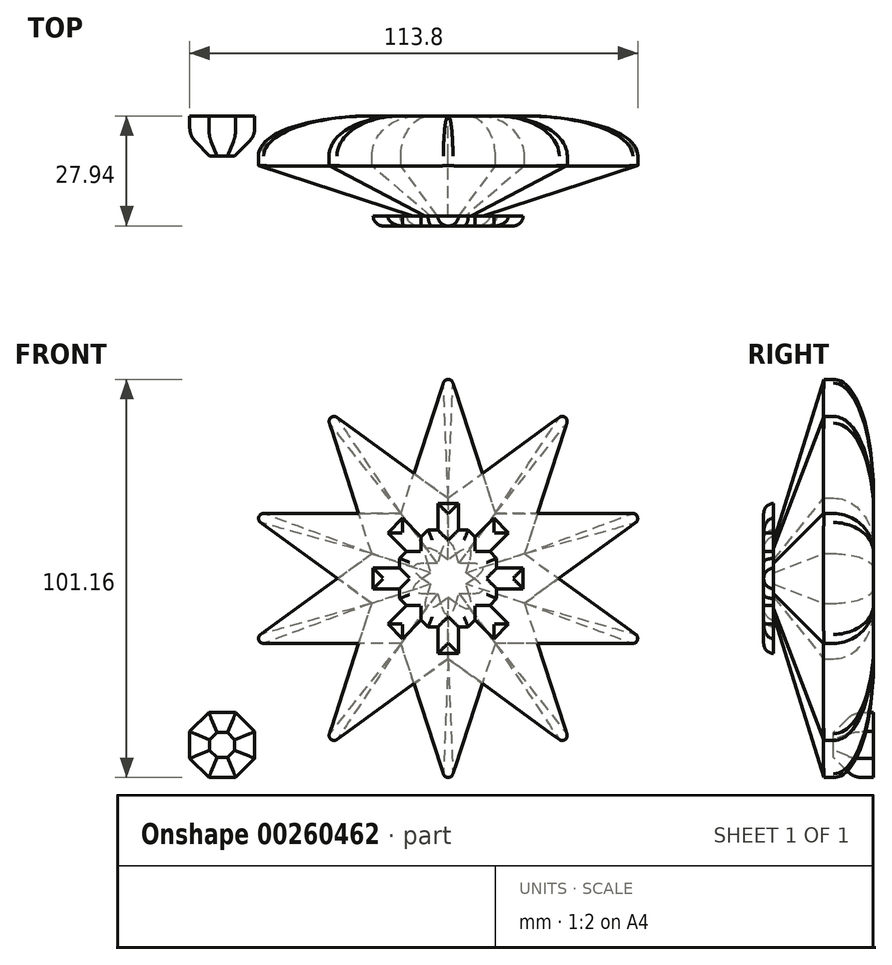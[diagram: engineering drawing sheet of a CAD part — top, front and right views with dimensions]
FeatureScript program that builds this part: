
annotation { "Feature Type Name" : "Feature", "Feature Type Description" : "" }
export const myFeature = defineFeature(function(context is Context, id is Id, definition is map)
    precondition{}
    {
        {
            var Q0;
            Q0=qCreatedBy(makeId("Front.planeOp"),FACE);
            var sketch = newSketch(context, id + "F0", { "sketchPlane" : qUnion([Q0])});
            skPoint(sketch, "E0.0.midPoint", {"position": v(0, 43.21) * mm});
            skLineSegment(sketch, "E1", {"start": v(50.8, -16.5) * mm, "end": v(-50.8, -16.5) * mm});
            skLineSegment(sketch, "E2", {"start": v(-50.8, -16.5) * mm, "end": v(31.4, 43.21) * mm});
            skLineSegment(sketch, "E3", {"start": v(31.4, 43.21) * mm, "end": v(0, -53.41) * mm});
            skLineSegment(sketch, "E4", {"start": v(0, -53.41) * mm, "end": v(-31.4, 43.21) * mm});
            skLineSegment(sketch, "E5", {"start": v(-31.4, 43.21) * mm, "end": v(50.8, -16.5) * mm});
            skSolve(sketch);
        }
        {
            var Q0;
            Q0=qCreatedBy(makeId("Front.planeOp"),FACE);
            var sketch = newSketch(context, id + "F1", { "sketchPlane" : qUnion([Q0])});
            skPoint(sketch, "E6.0.midPoint", {"position": v(0, -43.21) * mm});
            skLineSegment(sketch, "E7", {"start": v(-31.4, -43.21) * mm, "end": v(0, 53.41) * mm});
            skLineSegment(sketch, "E8", {"start": v(0, 53.41) * mm, "end": v(31.4, -43.21) * mm});
            skLineSegment(sketch, "E9", {"start": v(-50.8, 16.5) * mm, "end": v(31.4, -43.21) * mm});
            skLineSegment(sketch, "E10", {"start": v(50.8, 16.5) * mm, "end": v(-50.8, 16.5) * mm});
            skLineSegment(sketch, "E11", {"start": v(-31.4, -43.21) * mm, "end": v(50.8, 16.5) * mm});
            skSolve(sketch);
        }
        {
            var Q0;
            {var subQ0=sQuery(id+"F0.wireOp",EDGE,"E2");var subQ1=sQuery(id+"F0.wireOp",EDGE,"E1");var subQ2=makeQuery(id+"F0.imprint","INTERSECT",VERTEX,{"derivedFrom":[subQ1,subQ0]});Q0=makeQuery(id+"F0.imprint","IMPRINT",FACE,{"disambiguationData":[TD([[makeQuery(id+"F0.imprint","IMPRINT",EDGE,{"disambiguationData":[TD([[subQ2,1.0]])],"derivedFrom":subQ1}),-1.0]])]});}
            var Q1;
            {var subQ0=sQuery(id+"F0.wireOp",EDGE,"E4");var subQ1=sQuery(id+"F0.wireOp",EDGE,"E2");var subQ2=makeQuery(id+"F0.imprint","INTERSECT",VERTEX,{"derivedFrom":[subQ1,subQ0]});Q1=makeQuery(id+"F0.imprint","IMPRINT",FACE,{"disambiguationData":[TD([[makeQuery(id+"F0.imprint","IMPRINT",EDGE,{"disambiguationData":[TD([[subQ2,-1.0]])],"derivedFrom":subQ1}),1.0]])]});}
            var Q2;
            {var subQ1=sQuery(id+"F0.wireOp",EDGE,"E1");var subQ5=sQuery(id+"F0.wireOp",EDGE,"E3");var subQ6=makeQuery(id+"F0.imprint","INTERSECT",VERTEX,{"derivedFrom":[subQ1,subQ5]});Q2=makeQuery(id+"F0.imprint","IMPRINT",FACE,{"disambiguationData":[TD([[makeQuery(id+"F0.imprint","IMPRINT",EDGE,{"disambiguationData":[TD([[subQ6,-1.0]])],"derivedFrom":subQ1}),-1.0]])]});}
            var Q3;
            {var subQ0=sQuery(id+"F0.wireOp",EDGE,"E3");var subQ1=sQuery(id+"F0.wireOp",EDGE,"E2");var subQ2=makeQuery(id+"F0.imprint","INTERSECT",VERTEX,{"derivedFrom":[subQ1,subQ0]});Q3=makeQuery(id+"F0.imprint","IMPRINT",FACE,{"disambiguationData":[TD([[makeQuery(id+"F0.imprint","IMPRINT",EDGE,{"disambiguationData":[TD([[subQ2,1.0]])],"derivedFrom":subQ1}),-1.0]])]});}
            var Q4;
            {var subQ0=sQuery(id+"F0.wireOp",EDGE,"E5");var subQ1=sQuery(id+"F0.wireOp",EDGE,"E1");var subQ2=makeQuery(id+"F0.imprint","INTERSECT",VERTEX,{"derivedFrom":[subQ1,subQ0]});Q4=makeQuery(id+"F0.imprint","IMPRINT",FACE,{"disambiguationData":[TD([[makeQuery(id+"F0.imprint","IMPRINT",EDGE,{"disambiguationData":[TD([[subQ2,-1.0]])],"derivedFrom":subQ1}),-1.0]])]});}
            var Q5;
            {var subQ0=sQuery(id+"F0.wireOp",EDGE,"E3");var subQ1=sQuery(id+"F0.wireOp",EDGE,"E1");var subQ2=makeQuery(id+"F0.imprint","INTERSECT",VERTEX,{"derivedFrom":[subQ1,subQ0]});Q5=makeQuery(id+"F0.imprint","IMPRINT",FACE,{"disambiguationData":[TD([[makeQuery(id+"F0.imprint","IMPRINT",EDGE,{"disambiguationData":[TD([[subQ2,-1.0]])],"derivedFrom":subQ1}),1.0]])]});}
            extrude(context, id + "F2", {"entities" : qUnion([Q0, Q1, Q2, Q3, Q4, Q5]), "depth" : 25.4 * mm});
        }
        {
            var Q0;
            Q0=makeQuery(id+"F2.opExtrude","CAP_FACE",FACE,{"disambiguationData":[OSD([sQuery(id+"F0.wireOp",EDGE,"E1"),sQuery(id+"F0.wireOp",EDGE,"E2"),sQuery(id+"F0.wireOp",EDGE,"E3"),sQuery(id+"F0.wireOp",EDGE,"E4"),sQuery(id+"F0.wireOp",EDGE,"E5")])],"isStart":false});
            chamfer(context, id + "F3", {"entities" : qUnion([Q0]), "width" : 12.7 * mm, "tangentPropagation" : true});
        }
        {
            var Q0;
            {var subQ1=sQuery(id+"F1.wireOp",EDGE,"E7");var subQ7=sQuery(id+"F1.wireOp",EDGE,"E9");var subQ9=makeQuery(id+"F1.imprint","INTERSECT",VERTEX,{"derivedFrom":[subQ1,subQ7]});Q0=makeQuery(id+"F1.imprint","IMPRINT",FACE,{"disambiguationData":[TD([[makeQuery(id+"F1.imprint","IMPRINT",EDGE,{"disambiguationData":[TD([[subQ9,-1.0]])],"derivedFrom":subQ1}),-1.0]])]});}
            var Q1;
            {var subQ0=sQuery(id+"F1.wireOp",EDGE,"E10");var subQ1=sQuery(id+"F1.wireOp",EDGE,"E8");var subQ2=makeQuery(id+"F1.imprint","INTERSECT",VERTEX,{"derivedFrom":[subQ1,subQ0]});Q1=makeQuery(id+"F1.imprint","IMPRINT",FACE,{"disambiguationData":[TD([[makeQuery(id+"F1.imprint","IMPRINT",EDGE,{"disambiguationData":[TD([[subQ2,-1.0]])],"derivedFrom":subQ1}),1.0]])]});}
            var Q2;
            {var subQ0=sQuery(id+"F1.wireOp",EDGE,"E8");var subQ1=sQuery(id+"F1.wireOp",EDGE,"E7");var subQ2=makeQuery(id+"F1.imprint","INTERSECT",VERTEX,{"derivedFrom":[subQ1,subQ0]});Q2=makeQuery(id+"F1.imprint","IMPRINT",FACE,{"disambiguationData":[TD([[makeQuery(id+"F1.imprint","IMPRINT",EDGE,{"disambiguationData":[TD([[subQ2,1.0]])],"derivedFrom":subQ1}),-1.0]])]});}
            var Q3;
            {var subQ0=sQuery(id+"F1.wireOp",EDGE,"E9");var subQ1=sQuery(id+"F1.wireOp",EDGE,"E7");var subQ2=makeQuery(id+"F1.imprint","INTERSECT",VERTEX,{"derivedFrom":[subQ1,subQ0]});Q3=makeQuery(id+"F1.imprint","IMPRINT",FACE,{"disambiguationData":[TD([[makeQuery(id+"F1.imprint","IMPRINT",EDGE,{"disambiguationData":[TD([[subQ2,-1.0]])],"derivedFrom":subQ1}),1.0]])]});}
            var Q4;
            {var subQ0=sQuery(id+"F1.wireOp",EDGE,"E11");var subQ1=sQuery(id+"F1.wireOp",EDGE,"E7");var subQ2=makeQuery(id+"F1.imprint","INTERSECT",VERTEX,{"derivedFrom":[subQ1,subQ0]});Q4=makeQuery(id+"F1.imprint","IMPRINT",FACE,{"disambiguationData":[TD([[makeQuery(id+"F1.imprint","IMPRINT",EDGE,{"disambiguationData":[TD([[subQ2,-1.0]])],"derivedFrom":subQ1}),-1.0]])]});}
            var Q5;
            {var subQ0=sQuery(id+"F1.wireOp",EDGE,"E9");var subQ1=sQuery(id+"F1.wireOp",EDGE,"E8");var subQ2=makeQuery(id+"F1.imprint","INTERSECT",VERTEX,{"derivedFrom":[subQ1,subQ0]});Q5=makeQuery(id+"F1.imprint","IMPRINT",FACE,{"disambiguationData":[TD([[makeQuery(id+"F1.imprint","IMPRINT",EDGE,{"disambiguationData":[TD([[subQ2,1.0]])],"derivedFrom":subQ1}),-1.0]])]});}
            extrude(context, id + "F4", {"entities" : qUnion([Q0, Q1, Q2, Q3, Q4, Q5]), "depth" : 25.4 * mm});
        }
        {
            var Q0;
            Q0=makeQuery(id+"F4.opExtrude","CAP_FACE",FACE,{"disambiguationData":[OSD([sQuery(id+"F1.wireOp",EDGE,"E7"),sQuery(id+"F1.wireOp",EDGE,"E8"),sQuery(id+"F1.wireOp",EDGE,"E9"),sQuery(id+"F1.wireOp",EDGE,"E10"),sQuery(id+"F1.wireOp",EDGE,"E11")])],"isStart":false});
            chamfer(context, id + "F5", {"entities" : qUnion([Q0]), "width" : 12.7 * mm, "tangentPropagation" : true});
        }
        {
            var Q0;
            Q0=makeQuery(id+"F4.opExtrude","CAP_FACE",FACE,{"disambiguationData":[OSD([sQuery(id+"F1.wireOp",EDGE,"E7"),sQuery(id+"F1.wireOp",EDGE,"E8"),sQuery(id+"F1.wireOp",EDGE,"E9"),sQuery(id+"F1.wireOp",EDGE,"E10"),sQuery(id+"F1.wireOp",EDGE,"E11")])],"isStart":false});
            var sketch = newSketch(context, id + "F6", { "sketchPlane" : qUnion([Q0])});
            skCircle(sketch, "E12.cCircle", {"center": v(0, 0) * mm, "radius": 12.32 * mm, "construction": true});
            skLineSegment(sketch, "E12.0", {"start": v(-5.1, 12.32) * mm, "end": v(5.1, 12.32) * mm});
            skLineSegment(sketch, "E12.1", {"start": v(5.1, 12.32) * mm, "end": v(12.32, 5.1) * mm});
            skLineSegment(sketch, "E12.2", {"start": v(12.32, 5.1) * mm, "end": v(12.32, -5.1) * mm});
            skLineSegment(sketch, "E12.3", {"start": v(12.32, -5.1) * mm, "end": v(5.1, -12.32) * mm});
            skLineSegment(sketch, "E12.4", {"start": v(5.1, -12.32) * mm, "end": v(-5.1, -12.32) * mm});
            skLineSegment(sketch, "E12.5", {"start": v(-5.1, -12.32) * mm, "end": v(-12.32, -5.1) * mm});
            skLineSegment(sketch, "E12.6", {"start": v(-12.32, -5.1) * mm, "end": v(-12.32, 5.1) * mm});
            skLineSegment(sketch, "E12.7", {"start": v(-12.32, 5.1) * mm, "end": v(-5.1, 12.32) * mm});
            skPoint(sketch, "E12.0.midPoint", {"position": v(0, 12.32) * mm});
            skSolve(sketch);
        }
        {
            var Q0;
            {var subQ17=sQuery(id+"F6.wireOp",EDGE,"E12.1");Q0=makeQuery(id+"F6.imprint","IMPRINT",FACE,{"disambiguationData":[TD([[makeQuery(id+"F6.imprint","IMPRINT",EDGE,{"derivedFrom":subQ17}),-1.0]])]});}
            var Q1;
            {var subQ0=sQuery(id+"F1.wireOp",EDGE,"E11");var subQ1=sQuery(id+"F1.wireOp",EDGE,"E10");var subQ2=sQuery(id+"F1.wireOp",EDGE,"E9");var subQ3=sQuery(id+"F1.wireOp",EDGE,"E8");var subQ4=sQuery(id+"F1.wireOp",EDGE,"E7");var subQ5=makeQuery(id+"F4.opExtrude","CAP_FACE",FACE,{"disambiguationData":[OSD([subQ4,subQ3,subQ2,subQ1,subQ0])],"isStart":false});var subQ8=makeQuery(id+"F1.imprint","INTERSECT",VERTEX,{"derivedFrom":[subQ4,subQ0]});Q1=makeQuery(id+"F6.imprint","IMPRINT",FACE,{"disambiguationData":[TD([[makeQuery(id+"F6.imprint","IMPRINT",EDGE,{"derivedFrom":makeQuery(id+"F5.opChamfer","BLEND_EDGE",EDGE,{"blendedFrom":[makeQuery(id+"F4.opExtrude","CAP_EDGE",EDGE,{"disambiguationData":[OSD([subQ4]),TDD([makeQuery(id+"F1.imprint","IMPRINT",EDGE,{"disambiguationData":[TD([[subQ8,-1.0]])],"derivedFrom":subQ4})])],"isStart":false}),subQ5],"blendedInto":[subQ5]})}),1.0]])]});}
            extrude(context, id + "F7", {"entities" : qUnion([Q0, Q1]), "depth" : 2.54 * mm});
        }
        {
            var Q0;
            Q0=makeQuery(id+"F2.opExtrude","SWEPT_EDGE",EDGE,{"disambiguationData":[OSD([sQuery(id+"F0.wireOp",EDGE,"E2"),sQuery(id+"F0.wireOp",EDGE,"E3")])]});
            var Q1;
            Q1=makeQuery(id+"F4.opExtrude","SWEPT_EDGE",EDGE,{"disambiguationData":[OSD([sQuery(id+"F1.wireOp",EDGE,"E10"),sQuery(id+"F1.wireOp",EDGE,"E11")])]});
            var Q2;
            Q2=makeQuery(id+"F2.opExtrude","SWEPT_EDGE",EDGE,{"disambiguationData":[OSD([sQuery(id+"F0.wireOp",EDGE,"E1"),sQuery(id+"F0.wireOp",EDGE,"E5")])]});
            var Q3;
            Q3=makeQuery(id+"F4.opExtrude","SWEPT_EDGE",EDGE,{"disambiguationData":[OSD([sQuery(id+"F1.wireOp",EDGE,"E8"),sQuery(id+"F1.wireOp",EDGE,"E9")])]});
            var Q4;
            Q4=makeQuery(id+"F2.opExtrude","SWEPT_EDGE",EDGE,{"disambiguationData":[OSD([sQuery(id+"F0.wireOp",EDGE,"E3"),sQuery(id+"F0.wireOp",EDGE,"E4")])]});
            var Q5;
            Q5=makeQuery(id+"F4.opExtrude","SWEPT_EDGE",EDGE,{"disambiguationData":[OSD([sQuery(id+"F1.wireOp",EDGE,"E7"),sQuery(id+"F1.wireOp",EDGE,"E11")])]});
            var Q6;
            Q6=makeQuery(id+"F2.opExtrude","SWEPT_EDGE",EDGE,{"disambiguationData":[OSD([sQuery(id+"F0.wireOp",EDGE,"E1"),sQuery(id+"F0.wireOp",EDGE,"E2")])]});
            var Q7;
            Q7=makeQuery(id+"F4.opExtrude","SWEPT_EDGE",EDGE,{"disambiguationData":[OSD([sQuery(id+"F1.wireOp",EDGE,"E9"),sQuery(id+"F1.wireOp",EDGE,"E10")])]});
            var Q8;
            Q8=makeQuery(id+"F2.opExtrude","SWEPT_EDGE",EDGE,{"disambiguationData":[OSD([sQuery(id+"F0.wireOp",EDGE,"E4"),sQuery(id+"F0.wireOp",EDGE,"E5")])]});
            var Q9;
            Q9=makeQuery(id+"F4.opExtrude","SWEPT_EDGE",EDGE,{"disambiguationData":[OSD([sQuery(id+"F1.wireOp",EDGE,"E7"),sQuery(id+"F1.wireOp",EDGE,"E8")])]});
            fillet(context, id + "F8", {"entities" : qUnion([Q0, Q1, Q2, Q3, Q4, Q5, Q6, Q7, Q8, Q9]), "radius" : 1.27 * mm, "tangentPropagation" : true, "allowEdgeOverflow" : false});
        }
        {
            var Q0;
            {var subQ0=sQuery(id+"F0.wireOp",EDGE,"E4");var subQ1=sQuery(id+"F0.wireOp",EDGE,"E3");var subQ2=makeQuery(id+"F0.imprint","INTERSECT",VERTEX,{"derivedFrom":[subQ1,subQ0]});Q0=makeQuery(id+"F3.opChamfer","BLEND_EDGE",EDGE,{"blendedFrom":[makeQuery(id+"F2.opExtrude","CAP_EDGE",EDGE,{"disambiguationData":[OSD([subQ1]),TDD([makeQuery(id+"F0.imprint","IMPRINT",EDGE,{"disambiguationData":[TD([[subQ2,1.0]])],"derivedFrom":subQ1})])],"isStart":false}),makeQuery(id+"F2.opExtrude","CAP_EDGE",EDGE,{"disambiguationData":[OSD([subQ0]),TDD([makeQuery(id+"F0.imprint","IMPRINT",EDGE,{"disambiguationData":[TD([[subQ2,-1.0]])],"derivedFrom":subQ0})])],"isStart":false})],"blendedInto":[]});}
            var Q1;
            {var subQ0=sQuery(id+"F1.wireOp",EDGE,"E9");var subQ1=sQuery(id+"F1.wireOp",EDGE,"E8");var subQ2=makeQuery(id+"F1.imprint","INTERSECT",VERTEX,{"derivedFrom":[subQ1,subQ0]});Q1=makeQuery(id+"F5.opChamfer","BLEND_EDGE",EDGE,{"blendedFrom":[makeQuery(id+"F4.opExtrude","CAP_EDGE",EDGE,{"disambiguationData":[OSD([subQ1]),TDD([makeQuery(id+"F1.imprint","IMPRINT",EDGE,{"disambiguationData":[TD([[subQ2,1.0]])],"derivedFrom":subQ1})])],"isStart":false}),makeQuery(id+"F4.opExtrude","CAP_EDGE",EDGE,{"disambiguationData":[OSD([subQ0]),TDD([makeQuery(id+"F1.imprint","IMPRINT",EDGE,{"disambiguationData":[TD([[subQ2,1.0]])],"derivedFrom":subQ0})])],"isStart":false})],"blendedInto":[]});}
            var Q2;
            {var subQ0=sQuery(id+"F0.wireOp",EDGE,"E5");var subQ1=sQuery(id+"F0.wireOp",EDGE,"E1");var subQ2=makeQuery(id+"F0.imprint","INTERSECT",VERTEX,{"derivedFrom":[subQ1,subQ0]});Q2=makeQuery(id+"F3.opChamfer","BLEND_EDGE",EDGE,{"blendedFrom":[makeQuery(id+"F2.opExtrude","CAP_EDGE",EDGE,{"disambiguationData":[OSD([subQ1]),TDD([makeQuery(id+"F0.imprint","IMPRINT",EDGE,{"disambiguationData":[TD([[subQ2,-1.0]])],"derivedFrom":subQ1})])],"isStart":false}),makeQuery(id+"F2.opExtrude","CAP_EDGE",EDGE,{"disambiguationData":[OSD([subQ0]),TDD([makeQuery(id+"F0.imprint","IMPRINT",EDGE,{"disambiguationData":[TD([[subQ2,1.0]])],"derivedFrom":subQ0})])],"isStart":false})],"blendedInto":[]});}
            var Q3;
            {var subQ0=sQuery(id+"F1.wireOp",EDGE,"E11");var subQ1=sQuery(id+"F1.wireOp",EDGE,"E10");var subQ2=makeQuery(id+"F1.imprint","INTERSECT",VERTEX,{"derivedFrom":[subQ1,subQ0]});Q3=makeQuery(id+"F5.opChamfer","BLEND_EDGE",EDGE,{"blendedFrom":[makeQuery(id+"F4.opExtrude","CAP_EDGE",EDGE,{"disambiguationData":[OSD([subQ1]),TDD([makeQuery(id+"F1.imprint","IMPRINT",EDGE,{"disambiguationData":[TD([[subQ2,-1.0]])],"derivedFrom":subQ1})])],"isStart":false}),makeQuery(id+"F4.opExtrude","CAP_EDGE",EDGE,{"disambiguationData":[OSD([subQ0]),TDD([makeQuery(id+"F1.imprint","IMPRINT",EDGE,{"disambiguationData":[TD([[subQ2,1.0]])],"derivedFrom":subQ0})])],"isStart":false})],"blendedInto":[]});}
            var Q4;
            {var subQ0=sQuery(id+"F0.wireOp",EDGE,"E3");var subQ1=sQuery(id+"F0.wireOp",EDGE,"E2");var subQ2=makeQuery(id+"F0.imprint","INTERSECT",VERTEX,{"derivedFrom":[subQ1,subQ0]});Q4=makeQuery(id+"F3.opChamfer","BLEND_EDGE",EDGE,{"blendedFrom":[makeQuery(id+"F2.opExtrude","CAP_EDGE",EDGE,{"disambiguationData":[OSD([subQ1]),TDD([makeQuery(id+"F0.imprint","IMPRINT",EDGE,{"disambiguationData":[TD([[subQ2,1.0]])],"derivedFrom":subQ1})])],"isStart":false}),makeQuery(id+"F2.opExtrude","CAP_EDGE",EDGE,{"disambiguationData":[OSD([subQ0]),TDD([makeQuery(id+"F0.imprint","IMPRINT",EDGE,{"disambiguationData":[TD([[subQ2,-1.0]])],"derivedFrom":subQ0})])],"isStart":false})],"blendedInto":[]});}
            var Q5;
            {var subQ0=sQuery(id+"F1.wireOp",EDGE,"E8");var subQ1=sQuery(id+"F1.wireOp",EDGE,"E7");var subQ2=makeQuery(id+"F1.imprint","INTERSECT",VERTEX,{"derivedFrom":[subQ1,subQ0]});Q5=makeQuery(id+"F5.opChamfer","BLEND_EDGE",EDGE,{"blendedFrom":[makeQuery(id+"F4.opExtrude","CAP_EDGE",EDGE,{"disambiguationData":[OSD([subQ1]),TDD([makeQuery(id+"F1.imprint","IMPRINT",EDGE,{"disambiguationData":[TD([[subQ2,1.0]])],"derivedFrom":subQ1})])],"isStart":false}),makeQuery(id+"F4.opExtrude","CAP_EDGE",EDGE,{"disambiguationData":[OSD([subQ0]),TDD([makeQuery(id+"F1.imprint","IMPRINT",EDGE,{"disambiguationData":[TD([[subQ2,-1.0]])],"derivedFrom":subQ0})])],"isStart":false})],"blendedInto":[]});}
            var Q6;
            {var subQ0=sQuery(id+"F0.wireOp",EDGE,"E5");var subQ1=sQuery(id+"F0.wireOp",EDGE,"E4");var subQ2=makeQuery(id+"F0.imprint","INTERSECT",VERTEX,{"derivedFrom":[subQ1,subQ0]});Q6=makeQuery(id+"F3.opChamfer","BLEND_EDGE",EDGE,{"blendedFrom":[makeQuery(id+"F2.opExtrude","CAP_EDGE",EDGE,{"disambiguationData":[OSD([subQ1]),TDD([makeQuery(id+"F0.imprint","IMPRINT",EDGE,{"disambiguationData":[TD([[subQ2,1.0]])],"derivedFrom":subQ1})])],"isStart":false}),makeQuery(id+"F2.opExtrude","CAP_EDGE",EDGE,{"disambiguationData":[OSD([subQ0]),TDD([makeQuery(id+"F0.imprint","IMPRINT",EDGE,{"disambiguationData":[TD([[subQ2,-1.0]])],"derivedFrom":subQ0})])],"isStart":false})],"blendedInto":[]});}
            var Q7;
            {var subQ0=sQuery(id+"F1.wireOp",EDGE,"E10");var subQ1=sQuery(id+"F1.wireOp",EDGE,"E9");var subQ2=makeQuery(id+"F1.imprint","INTERSECT",VERTEX,{"derivedFrom":[subQ1,subQ0]});Q7=makeQuery(id+"F5.opChamfer","BLEND_EDGE",EDGE,{"blendedFrom":[makeQuery(id+"F4.opExtrude","CAP_EDGE",EDGE,{"disambiguationData":[OSD([subQ1]),TDD([makeQuery(id+"F1.imprint","IMPRINT",EDGE,{"disambiguationData":[TD([[subQ2,-1.0]])],"derivedFrom":subQ1})])],"isStart":false}),makeQuery(id+"F4.opExtrude","CAP_EDGE",EDGE,{"disambiguationData":[OSD([subQ0]),TDD([makeQuery(id+"F1.imprint","IMPRINT",EDGE,{"disambiguationData":[TD([[subQ2,1.0]])],"derivedFrom":subQ0})])],"isStart":false})],"blendedInto":[]});}
            var Q8;
            {var subQ0=sQuery(id+"F0.wireOp",EDGE,"E2");var subQ1=sQuery(id+"F0.wireOp",EDGE,"E1");var subQ2=makeQuery(id+"F0.imprint","INTERSECT",VERTEX,{"derivedFrom":[subQ1,subQ0]});Q8=makeQuery(id+"F3.opChamfer","BLEND_EDGE",EDGE,{"blendedFrom":[makeQuery(id+"F2.opExtrude","CAP_EDGE",EDGE,{"disambiguationData":[OSD([subQ1]),TDD([makeQuery(id+"F0.imprint","IMPRINT",EDGE,{"disambiguationData":[TD([[subQ2,1.0]])],"derivedFrom":subQ1})])],"isStart":false}),makeQuery(id+"F2.opExtrude","CAP_EDGE",EDGE,{"disambiguationData":[OSD([subQ0]),TDD([makeQuery(id+"F0.imprint","IMPRINT",EDGE,{"disambiguationData":[TD([[subQ2,-1.0]])],"derivedFrom":subQ0})])],"isStart":false})],"blendedInto":[]});}
            var Q9;
            {var subQ0=sQuery(id+"F1.wireOp",EDGE,"E11");var subQ1=sQuery(id+"F1.wireOp",EDGE,"E7");var subQ2=makeQuery(id+"F1.imprint","INTERSECT",VERTEX,{"derivedFrom":[subQ1,subQ0]});Q9=makeQuery(id+"F5.opChamfer","BLEND_EDGE",EDGE,{"blendedFrom":[makeQuery(id+"F4.opExtrude","CAP_EDGE",EDGE,{"disambiguationData":[OSD([subQ1]),TDD([makeQuery(id+"F1.imprint","IMPRINT",EDGE,{"disambiguationData":[TD([[subQ2,-1.0]])],"derivedFrom":subQ1})])],"isStart":false}),makeQuery(id+"F4.opExtrude","CAP_EDGE",EDGE,{"disambiguationData":[OSD([subQ0]),TDD([makeQuery(id+"F1.imprint","IMPRINT",EDGE,{"disambiguationData":[TD([[subQ2,-1.0]])],"derivedFrom":subQ0})])],"isStart":false})],"blendedInto":[]});}
            fillet(context, id + "F9", {"entities" : qUnion([Q0, Q1, Q2, Q3, Q4, Q5, Q6, Q7, Q8, Q9]), "radius" : 2.54 * mm, "tangentPropagation" : true, "allowEdgeOverflow" : false});
        }
        {
            var Q0;
            Q0=makeQuery(id+"F4.opExtrude","CAP_FACE",FACE,{"disambiguationData":[OSD([sQuery(id+"F1.wireOp",EDGE,"E7"),sQuery(id+"F1.wireOp",EDGE,"E8"),sQuery(id+"F1.wireOp",EDGE,"E9"),sQuery(id+"F1.wireOp",EDGE,"E10"),sQuery(id+"F1.wireOp",EDGE,"E11")])],"isStart":true});
            var Q1;
            Q1=makeQuery(id+"F2.opExtrude","CAP_FACE",FACE,{"disambiguationData":[OSD([sQuery(id+"F0.wireOp",EDGE,"E1"),sQuery(id+"F0.wireOp",EDGE,"E2"),sQuery(id+"F0.wireOp",EDGE,"E3"),sQuery(id+"F0.wireOp",EDGE,"E4"),sQuery(id+"F0.wireOp",EDGE,"E5")])],"isStart":true});
            fillet(context, id + "F10", {"entities" : qUnion([Q0, Q1]), "radius" : 10.16 * mm, "tangentPropagation" : true, "allowEdgeOverflow" : false});
        }
        {
            var Q0;
            Q0=qCreatedBy(makeId("Front.planeOp"),FACE);
            var sketch = newSketch(context, id + "F11", { "sketchPlane" : qUnion([Q0])});
            skCircle(sketch, "E13.cCircle", {"center": v(-57.38, -42.33) * mm, "radius": 8.26 * mm, "construction": true});
            skLineSegment(sketch, "E13.0", {"start": v(-60.8, -34.08) * mm, "end": v(-53.96, -34.08) * mm});
            skLineSegment(sketch, "E13.1", {"start": v(-53.96, -34.08) * mm, "end": v(-49.13, -38.92) * mm});
            skLineSegment(sketch, "E13.2", {"start": v(-49.13, -38.92) * mm, "end": v(-49.13, -45.75) * mm});
            skLineSegment(sketch, "E13.3", {"start": v(-49.13, -45.75) * mm, "end": v(-53.96, -50.59) * mm});
            skLineSegment(sketch, "E13.4", {"start": v(-53.96, -50.59) * mm, "end": v(-60.8, -50.59) * mm});
            skLineSegment(sketch, "E13.5", {"start": v(-60.8, -50.59) * mm, "end": v(-65.64, -45.75) * mm});
            skLineSegment(sketch, "E13.6", {"start": v(-65.64, -45.75) * mm, "end": v(-65.64, -38.92) * mm});
            skLineSegment(sketch, "E13.7", {"start": v(-65.64, -38.92) * mm, "end": v(-60.8, -34.08) * mm});
            skPoint(sketch, "E13.0.midPoint", {"position": v(-57.38, -34.08) * mm});
            skSolve(sketch);
        }
        {
            var Q0;
            Q0=makeQuery(id+"F11.imprint","IMPRINT",FACE,{"disambiguationData":[TD([[makeQuery(id+"F11.imprint","IMPRINT",EDGE,{"derivedFrom":sQuery(id+"F11.wireOp",EDGE,"E13.0")}),-1.0]])]});
            extrude(context, id + "F12", {"entities" : qUnion([Q0]), "depth" : 10.16 * mm});
        }
        {
            var Q0;
            Q0=makeQuery(id+"F12.opExtrude","CAP_EDGE",EDGE,{"disambiguationData":[OSD([sQuery(id+"F11.wireOp",EDGE,"E13.5")])],"isStart":false});
            var Q1;
            Q1=makeQuery(id+"F12.opExtrude","CAP_FACE",FACE,{"disambiguationData":[OSD([sQuery(id+"F11.wireOp",EDGE,"E13.0"),sQuery(id+"F11.wireOp",EDGE,"E13.1"),sQuery(id+"F11.wireOp",EDGE,"E13.2"),sQuery(id+"F11.wireOp",EDGE,"E13.3"),sQuery(id+"F11.wireOp",EDGE,"E13.4"),sQuery(id+"F11.wireOp",EDGE,"E13.5"),sQuery(id+"F11.wireOp",EDGE,"E13.6"),sQuery(id+"F11.wireOp",EDGE,"E13.7")])],"isStart":false});
            chamfer(context, id + "F13", {"entities" : qUnion([Q0, Q1]), "width" : 5.08 * mm, "tangentPropagation" : true});
        }
        {
            var Q0;
            {var subQ0=sQuery(id+"F11.wireOp",EDGE,"E13.1");Q0=makeQuery(id+"F13.opChamfer","BLEND_EDGE",EDGE,{"blendedFrom":[makeQuery(id+"F12.opExtrude","CAP_EDGE",EDGE,{"disambiguationData":[OSD([subQ0])],"isStart":false}),makeQuery(id+"F12.opExtrude","SWEPT_FACE",FACE,{"disambiguationData":[OSD([subQ0])]})],"blendedInto":[makeQuery(id+"F12.opExtrude","SWEPT_FACE",FACE,{"disambiguationData":[OSD([subQ0])]})]});}
            var Q1;
            {var subQ0=sQuery(id+"F11.wireOp",EDGE,"E13.2");Q1=makeQuery(id+"F13.opChamfer","BLEND_EDGE",EDGE,{"blendedFrom":[makeQuery(id+"F12.opExtrude","CAP_EDGE",EDGE,{"disambiguationData":[OSD([subQ0])],"isStart":false}),makeQuery(id+"F12.opExtrude","SWEPT_FACE",FACE,{"disambiguationData":[OSD([subQ0])]})],"blendedInto":[makeQuery(id+"F12.opExtrude","SWEPT_FACE",FACE,{"disambiguationData":[OSD([subQ0])]})]});}
            var Q2;
            {var subQ0=sQuery(id+"F11.wireOp",EDGE,"E13.3");Q2=makeQuery(id+"F13.opChamfer","BLEND_EDGE",EDGE,{"blendedFrom":[makeQuery(id+"F12.opExtrude","CAP_EDGE",EDGE,{"disambiguationData":[OSD([subQ0])],"isStart":false}),makeQuery(id+"F12.opExtrude","SWEPT_FACE",FACE,{"disambiguationData":[OSD([subQ0])]})],"blendedInto":[makeQuery(id+"F12.opExtrude","SWEPT_FACE",FACE,{"disambiguationData":[OSD([subQ0])]})]});}
            var Q3;
            {var subQ0=sQuery(id+"F11.wireOp",EDGE,"E13.4");Q3=makeQuery(id+"F13.opChamfer","BLEND_EDGE",EDGE,{"blendedFrom":[makeQuery(id+"F12.opExtrude","CAP_EDGE",EDGE,{"disambiguationData":[OSD([subQ0])],"isStart":false}),makeQuery(id+"F12.opExtrude","SWEPT_FACE",FACE,{"disambiguationData":[OSD([subQ0])]})],"blendedInto":[makeQuery(id+"F12.opExtrude","SWEPT_FACE",FACE,{"disambiguationData":[OSD([subQ0])]})]});}
            var Q4;
            {var subQ0=sQuery(id+"F11.wireOp",EDGE,"E13.5");Q4=makeQuery(id+"F13.opChamfer","BLEND_EDGE",EDGE,{"blendedFrom":[makeQuery(id+"F12.opExtrude","CAP_EDGE",EDGE,{"disambiguationData":[OSD([subQ0])],"isStart":false}),makeQuery(id+"F12.opExtrude","SWEPT_FACE",FACE,{"disambiguationData":[OSD([subQ0])]})],"blendedInto":[makeQuery(id+"F12.opExtrude","SWEPT_FACE",FACE,{"disambiguationData":[OSD([subQ0])]})]});}
            var Q5;
            {var subQ0=sQuery(id+"F11.wireOp",EDGE,"E13.6");Q5=makeQuery(id+"F13.opChamfer","BLEND_EDGE",EDGE,{"blendedFrom":[makeQuery(id+"F12.opExtrude","CAP_EDGE",EDGE,{"disambiguationData":[OSD([subQ0])],"isStart":false}),makeQuery(id+"F12.opExtrude","SWEPT_FACE",FACE,{"disambiguationData":[OSD([subQ0])]})],"blendedInto":[makeQuery(id+"F12.opExtrude","SWEPT_FACE",FACE,{"disambiguationData":[OSD([subQ0])]})]});}
            var Q6;
            {var subQ0=sQuery(id+"F11.wireOp",EDGE,"E13.7");Q6=makeQuery(id+"F13.opChamfer","BLEND_EDGE",EDGE,{"blendedFrom":[makeQuery(id+"F12.opExtrude","CAP_EDGE",EDGE,{"disambiguationData":[OSD([subQ0])],"isStart":false}),makeQuery(id+"F12.opExtrude","SWEPT_FACE",FACE,{"disambiguationData":[OSD([subQ0])]})],"blendedInto":[makeQuery(id+"F12.opExtrude","SWEPT_FACE",FACE,{"disambiguationData":[OSD([subQ0])]})]});}
            var Q7;
            {var subQ0=sQuery(id+"F11.wireOp",EDGE,"E13.0");Q7=makeQuery(id+"F13.opChamfer","BLEND_EDGE",EDGE,{"blendedFrom":[makeQuery(id+"F12.opExtrude","CAP_EDGE",EDGE,{"disambiguationData":[OSD([subQ0])],"isStart":false}),makeQuery(id+"F12.opExtrude","SWEPT_FACE",FACE,{"disambiguationData":[OSD([subQ0])]})],"blendedInto":[makeQuery(id+"F12.opExtrude","SWEPT_FACE",FACE,{"disambiguationData":[OSD([subQ0])]})]});}
            fillet(context, id + "F14", {"entities" : qUnion([Q0, Q1, Q2, Q3, Q4, Q5, Q6, Q7]), "radius" : 5.08 * mm, "tangentPropagation" : true, "allowEdgeOverflow" : false});
        }
        {
            var Q0;
            Q0=makeQuery(id+"F7.opExtrude","CAP_FACE",FACE,{"disambiguationData":[OSD([sQuery(id+"F6.wireOp",EDGE,"E12.0"),sQuery(id+"F6.wireOp",EDGE,"E12.1"),sQuery(id+"F6.wireOp",EDGE,"E12.2"),sQuery(id+"F6.wireOp",EDGE,"E12.3"),sQuery(id+"F6.wireOp",EDGE,"E12.4"),sQuery(id+"F6.wireOp",EDGE,"E12.5"),sQuery(id+"F6.wireOp",EDGE,"E12.6"),sQuery(id+"F6.wireOp",EDGE,"E12.7")])],"isStart":false});
            var sketch = newSketch(context, id + "F15", { "sketchPlane" : qUnion([Q0])});
            skCircle(sketch, "E14.cCircle", {"center": v(0, 0) * mm, "radius": 6.35 * mm, "construction": true});
            skLineSegment(sketch, "E14.0", {"start": v(-2.63, 6.35) * mm, "end": v(2.63, 6.35) * mm});
            skLineSegment(sketch, "E14.1", {"start": v(2.63, 6.35) * mm, "end": v(6.35, 2.63) * mm});
            skLineSegment(sketch, "E14.2", {"start": v(6.35, 2.63) * mm, "end": v(6.35, -2.63) * mm});
            skLineSegment(sketch, "E14.3", {"start": v(6.35, -2.63) * mm, "end": v(2.63, -6.35) * mm});
            skLineSegment(sketch, "E14.4", {"start": v(2.63, -6.35) * mm, "end": v(-2.63, -6.35) * mm});
            skLineSegment(sketch, "E14.5", {"start": v(-2.63, -6.35) * mm, "end": v(-6.35, -2.63) * mm});
            skLineSegment(sketch, "E14.6", {"start": v(-6.35, -2.63) * mm, "end": v(-6.35, 2.63) * mm});
            skLineSegment(sketch, "E14.7", {"start": v(-6.35, 2.63) * mm, "end": v(-2.63, 6.35) * mm});
            skPoint(sketch, "E14.0.midPoint", {"position": v(0, 6.35) * mm});
            skLineSegment(sketch, "E15", {"start": v(2.63, 6.35) * mm, "end": v(2.63, 31.75) * mm});
            skLineSegment(sketch, "E16", {"start": v(6.35, 2.63) * mm, "end": v(15.33, 11.61) * mm});
            skLineSegment(sketch, "E17", {"start": v(6.35, -2.63) * mm, "end": v(31.75, -2.63) * mm});
            skLineSegment(sketch, "E18", {"start": v(2.63, -6.35) * mm, "end": v(11.61, -15.33) * mm});
            skLineSegment(sketch, "E19", {"start": v(-2.63, -6.35) * mm, "end": v(-2.63, -17.02) * mm});
            skLineSegment(sketch, "E20", {"start": v(-6.35, -2.63) * mm, "end": v(-15.33, -11.61) * mm});
            skLineSegment(sketch, "E21", {"start": v(-6.35, 2.63) * mm, "end": v(-15.75, 2.63) * mm});
            skLineSegment(sketch, "E22", {"start": v(-2.63, 6.35) * mm, "end": v(-11.61, 15.33) * mm});
            skLineSegment(sketch, "E23.top", {"start": v(-2.63, 19.05) * mm, "end": v(2.63, 19.05) * mm});
            skLineSegment(sketch, "E23.left", {"start": v(-2.63, 6.35) * mm, "end": v(-2.63, 19.05) * mm});
            skLineSegment(sketch, "E23.right", {"start": v(2.63, 6.35) * mm, "end": v(2.63, 19.05) * mm});
            skLineSegment(sketch, "E24.bottom", {"start": v(6.35, 2.63) * mm, "end": v(19.05, 2.63) * mm});
            skLineSegment(sketch, "E24.top", {"start": v(6.35, -2.63) * mm, "end": v(19.05, -2.63) * mm});
            skLineSegment(sketch, "E24.right", {"start": v(19.05, 2.63) * mm, "end": v(19.05, -2.63) * mm});
            skLineSegment(sketch, "E25.top", {"start": v(2.63, -19.05) * mm, "end": v(-2.63, -19.05) * mm});
            skLineSegment(sketch, "E25.left", {"start": v(2.63, -6.35) * mm, "end": v(2.63, -19.05) * mm});
            skLineSegment(sketch, "E25.right", {"start": v(-2.63, -6.35) * mm, "end": v(-2.63, -19.05) * mm});
            skLineSegment(sketch, "E26.bottom", {"start": v(-6.35, -2.63) * mm, "end": v(-19.05, -2.63) * mm});
            skLineSegment(sketch, "E26.top", {"start": v(-6.35, 2.63) * mm, "end": v(-19.05, 2.63) * mm});
            skLineSegment(sketch, "E26.right", {"start": v(-19.05, -2.63) * mm, "end": v(-19.05, 2.63) * mm});
            skLineSegment(sketch, "E27", {"start": v(-15.33, -11.61) * mm, "end": v(-9.13, -17.81) * mm});
            skLineSegment(sketch, "E28", {"start": v(11.61, -15.33) * mm, "end": v(17.02, -9.92) * mm});
            skLineSegment(sketch, "E29", {"start": v(15.33, 11.61) * mm, "end": v(9.7, 17.24) * mm});
            skLineSegment(sketch, "E30", {"start": v(-11.61, 15.33) * mm, "end": v(-17.44, 9.5) * mm});
            skLineSegment(sketch, "E31", {"start": v(2.63, 6.35) * mm, "end": v(11.61, 15.33) * mm});
            skLineSegment(sketch, "E32", {"start": v(-6.35, 2.63) * mm, "end": v(-15.33, 11.61) * mm});
            skLineSegment(sketch, "E33", {"start": v(6.35, -2.63) * mm, "end": v(17.02, -13.3) * mm});
            skLineSegment(sketch, "E34", {"start": v(-2.63, -6.35) * mm, "end": v(-11.61, -15.33) * mm});
            skSolve(sketch);
        }
        {
            var Q0;
            {var subQ0=sQuery(id+"F15.wireOp",EDGE,"E29");var subQ1=sQuery(id+"F15.wireOp",EDGE,"E16");var subQ2=makeQuery(id+"F15.imprint","INTERSECT",VERTEX,{"derivedFrom":[subQ1,subQ0]});Q0=makeQuery(id+"F15.imprint","IMPRINT",FACE,{"disambiguationData":[TD([[makeQuery(id+"F15.imprint","IMPRINT",EDGE,{"disambiguationData":[TD([[subQ2,1.0]])],"derivedFrom":subQ1}),1.0]])]});}
            var Q1;
            {var subQ0=sQuery(id+"F15.wireOp",EDGE,"E24.right");Q1=makeQuery(id+"F15.imprint","IMPRINT",FACE,{"disambiguationData":[TD([[makeQuery(id+"F15.imprint","IMPRINT",EDGE,{"derivedFrom":subQ0}),-1.0]])]});}
            var Q2;
            {var subQ0=sQuery(id+"F15.wireOp",EDGE,"E28");var subQ1=sQuery(id+"F15.wireOp",EDGE,"E18");var subQ2=makeQuery(id+"F15.imprint","INTERSECT",VERTEX,{"derivedFrom":[subQ1,subQ0]});Q2=makeQuery(id+"F15.imprint","IMPRINT",FACE,{"disambiguationData":[TD([[makeQuery(id+"F15.imprint","IMPRINT",EDGE,{"disambiguationData":[TD([[subQ2,1.0]])],"derivedFrom":subQ1}),1.0]])]});}
            var Q3;
            {var subQ0=sQuery(id+"F15.wireOp",EDGE,"E25.top");Q3=makeQuery(id+"F15.imprint","IMPRINT",FACE,{"disambiguationData":[TD([[makeQuery(id+"F15.imprint","IMPRINT",EDGE,{"derivedFrom":subQ0}),-1.0]])]});}
            var Q4;
            {var subQ0=sQuery(id+"F15.wireOp",EDGE,"E27");var subQ1=sQuery(id+"F15.wireOp",EDGE,"E20");var subQ2=makeQuery(id+"F15.imprint","INTERSECT",VERTEX,{"derivedFrom":[subQ1,subQ0]});Q4=makeQuery(id+"F15.imprint","IMPRINT",FACE,{"disambiguationData":[TD([[makeQuery(id+"F15.imprint","IMPRINT",EDGE,{"disambiguationData":[TD([[subQ2,1.0]])],"derivedFrom":subQ1}),1.0]])]});}
            var Q5;
            {var subQ0=sQuery(id+"F15.wireOp",EDGE,"E26.right");Q5=makeQuery(id+"F15.imprint","IMPRINT",FACE,{"disambiguationData":[TD([[makeQuery(id+"F15.imprint","IMPRINT",EDGE,{"derivedFrom":subQ0}),-1.0]])]});}
            var Q6;
            {var subQ0=sQuery(id+"F15.wireOp",EDGE,"E30");var subQ1=sQuery(id+"F15.wireOp",EDGE,"E22");var subQ2=makeQuery(id+"F15.imprint","INTERSECT",VERTEX,{"derivedFrom":[subQ1,subQ0]});Q6=makeQuery(id+"F15.imprint","IMPRINT",FACE,{"disambiguationData":[TD([[makeQuery(id+"F15.imprint","IMPRINT",EDGE,{"disambiguationData":[TD([[subQ2,1.0]])],"derivedFrom":subQ1}),1.0]])]});}
            var Q7;
            {var subQ0=sQuery(id+"F15.wireOp",EDGE,"E23.top");Q7=makeQuery(id+"F15.imprint","IMPRINT",FACE,{"disambiguationData":[TD([[makeQuery(id+"F15.imprint","IMPRINT",EDGE,{"derivedFrom":subQ0}),-1.0]])]});}
            extrude(context, id + "F16", {"entities" : qUnion([Q0, Q1, Q2, Q3, Q4, Q5, Q6, Q7]), "operationType" : NewBodyOperationType.ADD, "oppositeDirection" : true, "depth" : 2.54 * mm});
        }
        {
            var Q0;
            {var subQ0=sQuery(id+"F6.wireOp",EDGE,"E12.6");var subQ1=sQuery(id+"F6.wireOp",EDGE,"E12.4");var subQ2=sQuery(id+"F6.wireOp",EDGE,"E12.2");var subQ3=sQuery(id+"F6.wireOp",EDGE,"E12.0");var subQ4=sQuery(id+"F6.wireOp",EDGE,"E12.7");var subQ5=sQuery(id+"F6.wireOp",EDGE,"E12.5");var subQ6=sQuery(id+"F6.wireOp",EDGE,"E12.3");var subQ7=sQuery(id+"F6.wireOp",EDGE,"E12.1");Q0=makeQuery(id+"F16.boolean.opBoolean","MERGE",FACE,{"derivedFrom":[makeQuery(id+"F7.opExtrude","CAP_FACE",FACE,{"disambiguationData":[OSD([subQ3,subQ7,subQ2,subQ6,subQ1,subQ5,subQ0,subQ4])],"isStart":false}),makeQuery(id+"F16.opExtrude","CAP_FACE",FACE,{"disambiguationData":[OSD([subQ7,sQuery(id+"F15.wireOp",EDGE,"E16"),sQuery(id+"F15.wireOp",EDGE,"E29"),sQuery(id+"F15.wireOp",EDGE,"E31")])],"isStart":true}),makeQuery(id+"F16.opExtrude","CAP_FACE",FACE,{"disambiguationData":[OSD([subQ6,sQuery(id+"F15.wireOp",EDGE,"E18"),sQuery(id+"F15.wireOp",EDGE,"E28"),sQuery(id+"F15.wireOp",EDGE,"E33")])],"isStart":true}),makeQuery(id+"F16.opExtrude","CAP_FACE",FACE,{"disambiguationData":[OSD([subQ5,sQuery(id+"F15.wireOp",EDGE,"E20"),sQuery(id+"F15.wireOp",EDGE,"E27"),sQuery(id+"F15.wireOp",EDGE,"E34")])],"isStart":true}),makeQuery(id+"F16.opExtrude","CAP_FACE",FACE,{"disambiguationData":[OSD([subQ4,sQuery(id+"F15.wireOp",EDGE,"E22"),sQuery(id+"F15.wireOp",EDGE,"E30"),sQuery(id+"F15.wireOp",EDGE,"E32")])],"isStart":true}),makeQuery(id+"F16.opExtrude","CAP_FACE",FACE,{"disambiguationData":[OSD([subQ3,sQuery(id+"F15.wireOp",EDGE,"E23.top"),sQuery(id+"F15.wireOp",EDGE,"E23.left"),sQuery(id+"F15.wireOp",EDGE,"E23.right")])],"isStart":true}),makeQuery(id+"F16.opExtrude","CAP_FACE",FACE,{"disambiguationData":[OSD([subQ2,sQuery(id+"F15.wireOp",EDGE,"E24.bottom"),sQuery(id+"F15.wireOp",EDGE,"E24.top"),sQuery(id+"F15.wireOp",EDGE,"E24.right")])],"isStart":true}),makeQuery(id+"F16.opExtrude","CAP_FACE",FACE,{"disambiguationData":[OSD([subQ1,sQuery(id+"F15.wireOp",EDGE,"E25.top"),sQuery(id+"F15.wireOp",EDGE,"E25.left"),sQuery(id+"F15.wireOp",EDGE,"E25.right")])],"isStart":true}),makeQuery(id+"F16.opExtrude","CAP_FACE",FACE,{"disambiguationData":[OSD([subQ0,sQuery(id+"F15.wireOp",EDGE,"E26.bottom"),sQuery(id+"F15.wireOp",EDGE,"E26.top"),sQuery(id+"F15.wireOp",EDGE,"E26.right")])],"isStart":true})]});}
            fillet(context, id + "F17", {"entities" : qUnion([Q0]), "radius" : 2.54 * mm, "tangentPropagation" : true, "allowEdgeOverflow" : false});
        }
    });
